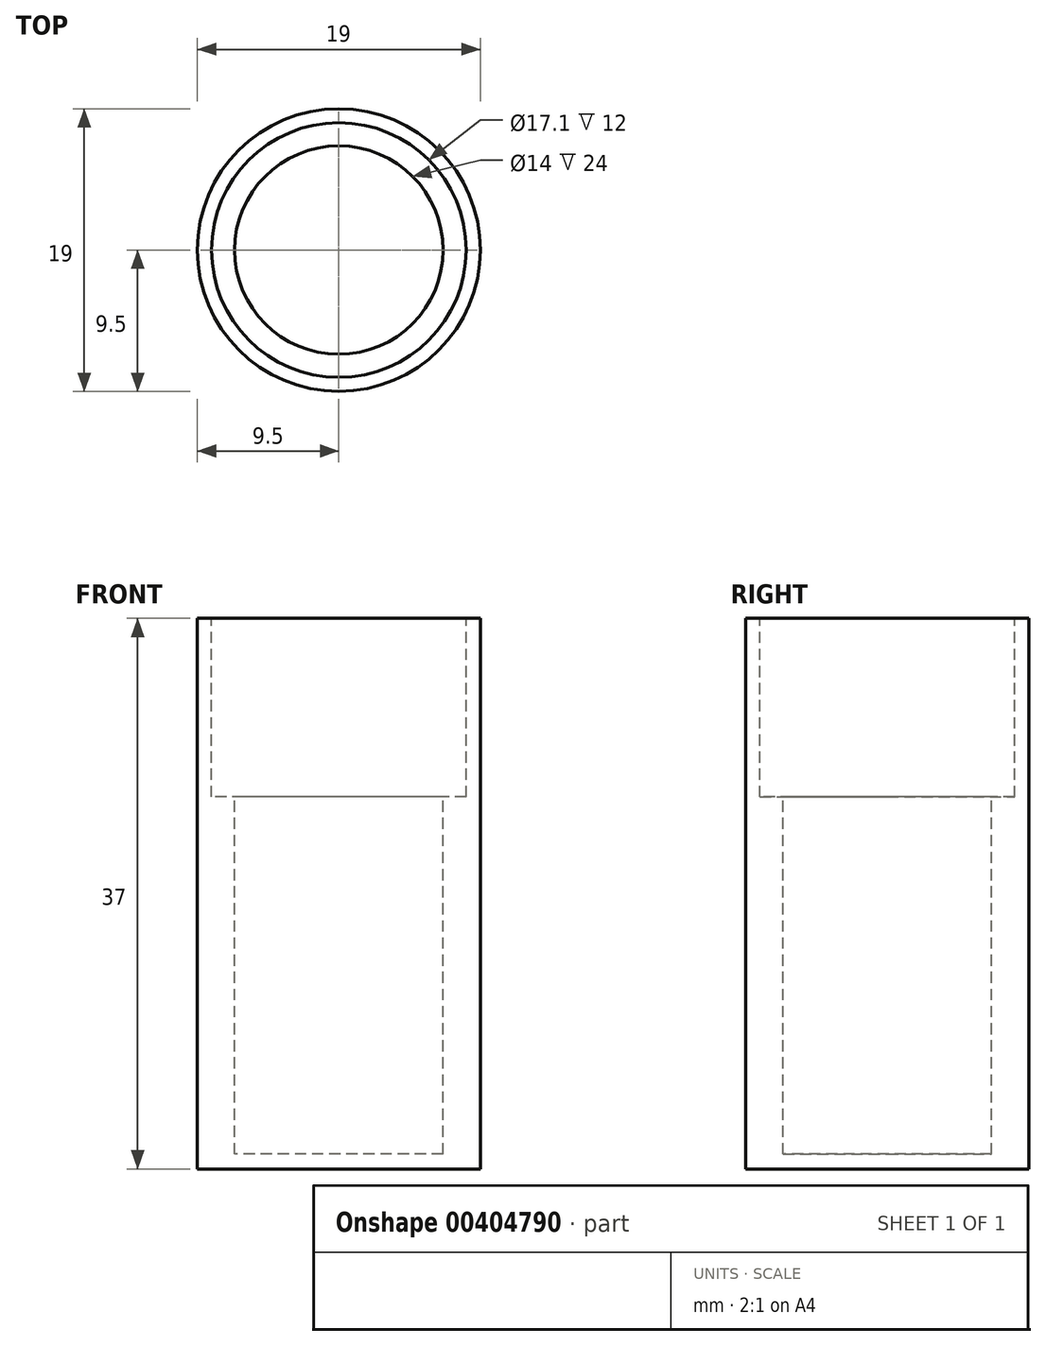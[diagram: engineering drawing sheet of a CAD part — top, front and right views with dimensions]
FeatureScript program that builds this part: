
annotation { "Feature Type Name" : "Feature", "Feature Type Description" : "" }
export const myFeature = defineFeature(function(context is Context, id is Id, definition is map)
    precondition{}
    {
        {
            var Q0;
            Q0=qCreatedBy(makeId("Top.planeOp"),FACE);
            var sketch = newSketch(context, id + "F0", { "sketchPlane" : qUnion([Q0])});
            skCircle(sketch, "E0", {"center": v(0, 0) * mm, "radius": 9.5 * mm});
            skSolve(sketch);
        }
        {
            var Q0;
            Q0=makeQuery(id+"F0.imprint","IMPRINT",FACE,{"disambiguationData":[TD([[makeQuery(id+"F0.imprint","IMPRINT",EDGE,{"derivedFrom":sQuery(id+"F0.wireOp",EDGE,"E0")}),1.0]])]});
            extrude(context, id + "F1", {"entities" : qUnion([Q0]), "depth" : 37 * mm});
        }
        {
            var Q0;
            Q0=makeQuery(id+"F1.opExtrude","CAP_FACE",FACE,{"disambiguationData":[OSD([sQuery(id+"F0.wireOp",EDGE,"E0")])],"isStart":false});
            var sketch = newSketch(context, id + "F2", { "sketchPlane" : qUnion([Q0])});
            skCircle(sketch, "E1", {"center": v(0, 0) * mm, "radius": 8.55 * mm});
            skCircle(sketch, "E2", {"center": v(0, 0) * mm, "radius": 7 * mm});
            skSolve(sketch);
        }
        {
            var Q0;
            Q0=makeQuery(id+"F2.imprint","IMPRINT",FACE,{"disambiguationData":[TD([[makeQuery(id+"F2.imprint","IMPRINT",EDGE,{"derivedFrom":sQuery(id+"F2.wireOp",EDGE,"E2")}),1.0]])]});
            extrude(context, id + "F3", {"entities" : qUnion([Q0]), "operationType" : NewBodyOperationType.REMOVE, "oppositeDirection" : true, "depth" : 36 * mm});
        }
        {
            var Q0;
            Q0=makeQuery(id+"F2.imprint","IMPRINT",FACE,{"disambiguationData":[TD([[makeQuery(id+"F2.imprint","IMPRINT",EDGE,{"derivedFrom":sQuery(id+"F2.wireOp",EDGE,"E1")}),1.0]])]});
            extrude(context, id + "F4", {"entities" : qUnion([Q0]), "operationType" : NewBodyOperationType.REMOVE, "oppositeDirection" : true, "depth" : 12 * mm});
        }
    });
